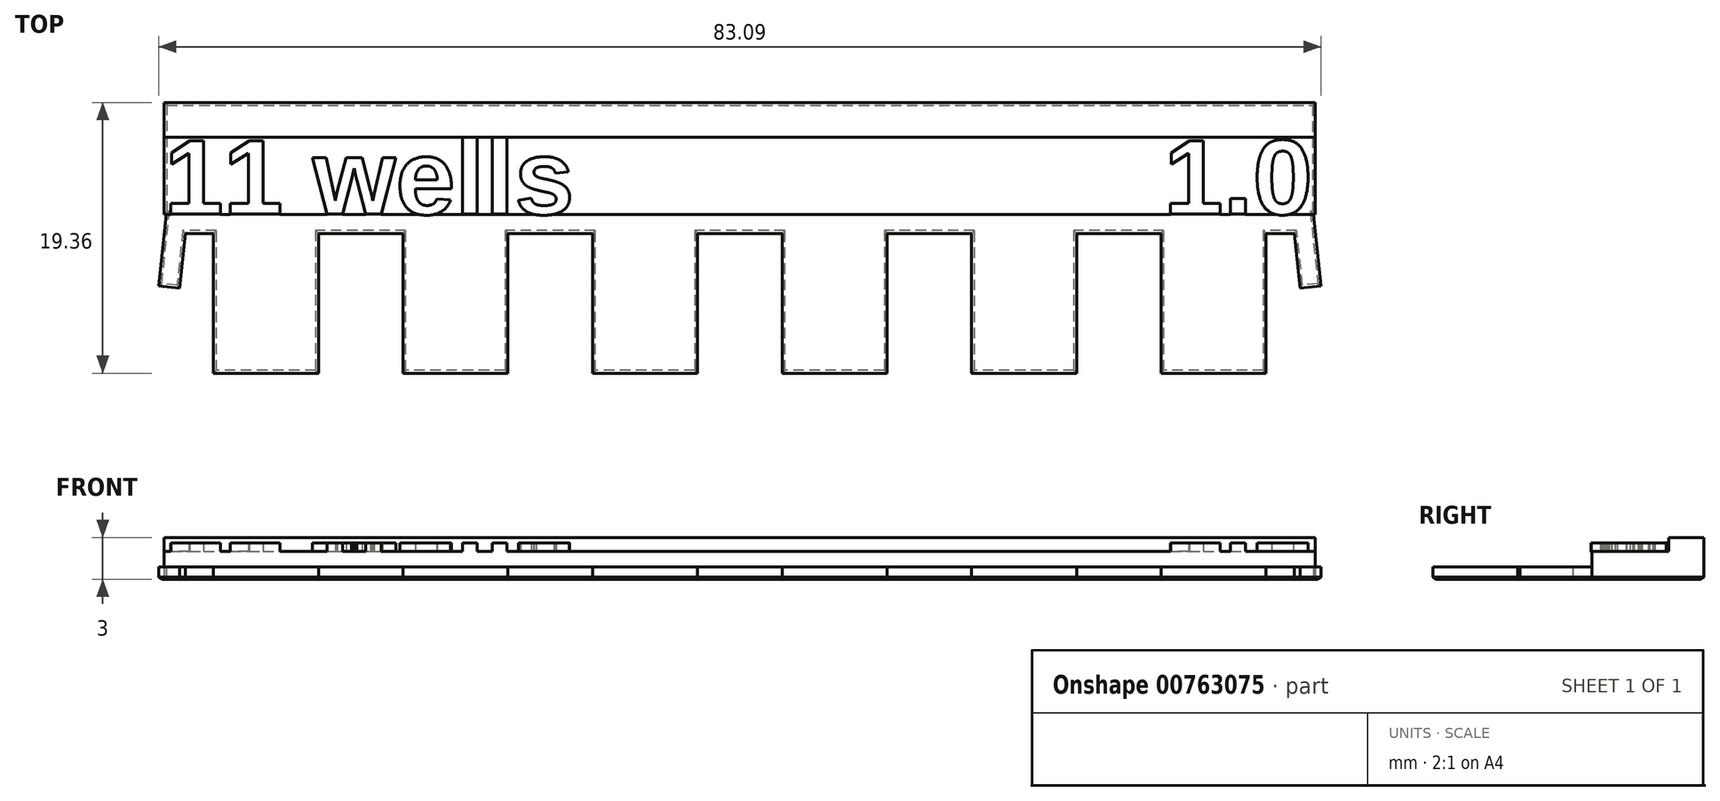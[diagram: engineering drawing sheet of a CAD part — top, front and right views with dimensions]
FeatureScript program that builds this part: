
annotation { "Feature Type Name" : "Feature", "Feature Type Description" : "" }
export const myFeature = defineFeature(function(context is Context, id is Id, definition is map)
    precondition{}
    {
        {
            assignVariable(context, id + "F0", {"name" : "thickness", "anyValue" : 0.9});
        }
        {
            var Q0;
            Q0=qCreatedBy(makeId("Top.planeOp"),FACE);
            var sketch = newSketch(context, id + "F1", { "sketchPlane" : qUnion([Q0])});
            skLineSegment(sketch, "E0", {"start": v(-32.04, 5.13) * mm, "end": v(-32.04, -4.87) * mm});
            skLineSegment(sketch, "E1", {"start": v(-32.04, -4.87) * mm, "end": v(-24.54, -4.87) * mm});
            skLineSegment(sketch, "E2", {"start": v(-24.54, -4.87) * mm, "end": v(-24.54, 5.13) * mm});
            skLineSegment(sketch, "E3", {"start": v(-24.54, 5.13) * mm, "end": v(-18.5, 5.13) * mm});
            skLineSegment(sketch, "E4", {"start": v(-35.57, 6.5) * mm, "end": v(46.73, 6.5) * mm});
            skLineSegment(sketch, "E5", {"start": v(-35.57, 12) * mm, "end": v(46.73, 12) * mm});
            skLineSegment(sketch, "E6", {"start": v(46.73, 14.5) * mm, "end": v(-35.57, 14.5) * mm});
            skLineSegment(sketch, "E7", {"start": v(-35.42, 6.5) * mm, "end": v(-35.57, 5.1) * mm});
            skLineSegment(sketch, "E8", {"start": v(-35.57, 5.1) * mm, "end": v(-35.96, 1.36) * mm});
            skLineSegment(sketch, "E9", {"start": v(-35.96, 1.36) * mm, "end": v(-34.47, 1.2) * mm});
            skLineSegment(sketch, "E10", {"start": v(5.58, 19.52) * mm, "end": v(5.58, -11.2) * mm, "construction": true});
            skLineSegment(sketch, "E11", {"start": v(-34.47, 1.2) * mm, "end": v(-34.05, 5.13) * mm});
            skLineSegment(sketch, "E12", {"start": v(-32.04, 5.13) * mm, "end": v(-34.05, 5.13) * mm});
            skLineSegment(sketch, "E13.1.0.0", {"start": v(-18.5, 5.13) * mm, "end": v(-18.5, -4.87) * mm});
            skLineSegment(sketch, "E13.1.0.1", {"start": v(-18.5, -4.87) * mm, "end": v(-11, -4.87) * mm});
            skLineSegment(sketch, "E13.1.0.2", {"start": v(-11, -4.87) * mm, "end": v(-11, 5.13) * mm});
            skLineSegment(sketch, "E13.1.0.3", {"start": v(-11, 5.13) * mm, "end": v(-4.94, 5.13) * mm});
            skLineSegment(sketch, "E13.2.0.0", {"start": v(-4.94, 5.13) * mm, "end": v(-4.94, -4.87) * mm});
            skLineSegment(sketch, "E13.2.0.1", {"start": v(-4.94, -4.87) * mm, "end": v(2.56, -4.87) * mm});
            skLineSegment(sketch, "E13.2.0.2", {"start": v(2.56, -4.87) * mm, "end": v(2.56, 5.13) * mm});
            skLineSegment(sketch, "E13.2.0.3", {"start": v(2.56, 5.13) * mm, "end": v(8.6, 5.13) * mm});
            skLineSegment(sketch, "E13.3.0.0", {"start": v(8.6, 5.13) * mm, "end": v(8.6, -4.87) * mm});
            skLineSegment(sketch, "E13.3.0.1", {"start": v(8.6, -4.87) * mm, "end": v(16.1, -4.87) * mm});
            skLineSegment(sketch, "E13.3.0.2", {"start": v(16.1, -4.87) * mm, "end": v(16.1, 5.13) * mm});
            skLineSegment(sketch, "E13.3.0.3", {"start": v(16.1, 5.13) * mm, "end": v(22.16, 5.13) * mm});
            skLineSegment(sketch, "E13.4.0.0", {"start": v(22.16, 5.13) * mm, "end": v(22.16, -4.87) * mm});
            skLineSegment(sketch, "E13.4.0.1", {"start": v(22.16, -4.87) * mm, "end": v(29.66, -4.87) * mm});
            skLineSegment(sketch, "E13.4.0.2", {"start": v(29.66, -4.87) * mm, "end": v(29.66, 5.13) * mm});
            skLineSegment(sketch, "E13.4.0.3", {"start": v(29.66, 5.13) * mm, "end": v(35.7, 5.13) * mm});
            skLineSegment(sketch, "E13.direction1", {"start": v(-32.04, -4.87) * mm, "end": v(-18.5, -4.87) * mm, "construction": true});
            skLineSegment(sketch, "E14", {"start": v(46.73, 6.5) * mm, "end": v(46.73, 14.5) * mm});
            skPoint(sketch, "E15", {"position": v(-35.57, 6.5) * mm});
            skLineSegment(sketch, "E16", {"start": v(-35.57, 12) * mm, "end": v(-35.57, 6.5) * mm});
            skLineSegment(sketch, "E17", {"start": v(-35.57, 12) * mm, "end": v(-35.57, 14.5) * mm});
            skLineSegment(sketch, "E18.MirrorCS", {"start": v(46.59, 6.5) * mm, "end": v(46.73, 5.1) * mm});
            skLineSegment(sketch, "E19.MirrorCS", {"start": v(46.73, 5.1) * mm, "end": v(47.13, 1.36) * mm});
            skLineSegment(sketch, "E20.MirrorCS", {"start": v(47.13, 1.36) * mm, "end": v(45.63, 1.2) * mm});
            skLineSegment(sketch, "E21.MirrorCS", {"start": v(45.63, 1.2) * mm, "end": v(45.22, 5.13) * mm});
            skLineSegment(sketch, "E22.MirrorCS", {"start": v(43.2, 5.13) * mm, "end": v(45.22, 5.13) * mm});
            skLineSegment(sketch, "E23.MirrorCS", {"start": v(43.2, 5.13) * mm, "end": v(43.2, -4.87) * mm});
            skLineSegment(sketch, "E24.MirrorCS", {"start": v(43.2, -4.87) * mm, "end": v(35.7, -4.87) * mm});
            skLineSegment(sketch, "E25.MirrorCS", {"start": v(35.7, -4.87) * mm, "end": v(35.7, 5.13) * mm});
            skSolve(sketch);
        }
        {
            var Q0;
            Q0=makeQuery(id+"F1.imprint","IMPRINT",FACE,{"disambiguationData":[TD([[makeQuery(id+"F1.imprint","IMPRINT",EDGE,{"derivedFrom":sQuery(id+"F1.wireOp",EDGE,"E0")}),1.0]])]});
            extrude(context, id + "F2", {"entities" : qUnion([Q0]), "depth" : (getVariable(context, 'thickness')) * mm, "offsetDistance" : 25 * mm});
        }
        {
            var Q0;
            {var subQ0=sQuery(id+"F1.wireOp",EDGE,"E5");Q0=makeQuery(id+"F1.imprint","IMPRINT",FACE,{"disambiguationData":[TD([[makeQuery(id+"F1.imprint","IMPRINT",EDGE,{"derivedFrom":subQ0}),-1.0]])]});}
            extrude(context, id + "F3", {"entities" : qUnion([Q0]), "operationType" : NewBodyOperationType.ADD, "depth" : 2 * mm, "offsetDistance" : 25 * mm});
        }
        {
            var Q0;
            {var subQ0=sQuery(id+"F1.wireOp",EDGE,"E5");Q0=makeQuery(id+"F1.imprint","IMPRINT",FACE,{"disambiguationData":[TD([[makeQuery(id+"F1.imprint","IMPRINT",EDGE,{"derivedFrom":subQ0}),1.0]])]});}
            extrude(context, id + "F4", {"entities" : qUnion([Q0]), "operationType" : NewBodyOperationType.ADD, "depth" : 3 * mm, "offsetDistance" : 25 * mm});
        }
        {
            var Q0;
            Q0=makeQuery(id+"F3.opExtrude","CAP_FACE",FACE,{"disambiguationData":[OSD([sQuery(id+"F1.wireOp",EDGE,"E4"),sQuery(id+"F1.wireOp",EDGE,"E5"),sQuery(id+"F1.wireOp",EDGE,"E14"),sQuery(id+"F1.wireOp",EDGE,"E16")])],"isStart":false});
            var sketch = newSketch(context, id + "F5", { "sketchPlane" : qUnion([Q0])});
            skText(sketch, "E26", { "text": "1.0", "fontName": "Arimo-Bold.ttf"});
            skText(sketch, "E27", { "text": "11 wells", "fontName": "Arimo-Bold.ttf"});
            const initialGuessF5  = {"E26": [0.0359, 0.0065, 1, 0, 0.0055], "E27": [-0.03557, 0.0065, 1, 0, 0.0055]};
            skSetInitialGuess(sketch, initialGuessF5);
            skSolve(sketch);
        }
        {
            var Q0;
            Q0 = qSketchRegion(id + "F5", true);
            extrude(context, id + "F6", {"entities" : qUnion([Q0]), "operationType" : NewBodyOperationType.ADD, "depth" : 0.6 * mm, "offsetDistance" : 25 * mm});
        }
        {
            var Q0;
            {var subQ0=sQuery(id+"F1.wireOp",EDGE,"E14");var subQ1=sQuery(id+"F1.wireOp",EDGE,"E5");var subQ2=sQuery(id+"F1.wireOp",EDGE,"E4");Q0=makeQuery(id+"F4.boolean.opBoolean","MERGE",FACE,{"derivedFrom":[makeQuery(id+"F3.boolean.opBoolean","MERGE",FACE,{"derivedFrom":[makeQuery(id+"F2.opExtrude","CAP_FACE",FACE,{"disambiguationData":[OSD([sQuery(id+"F1.wireOp",EDGE,"E0"),sQuery(id+"F1.wireOp",EDGE,"E1"),sQuery(id+"F1.wireOp",EDGE,"E2"),sQuery(id+"F1.wireOp",EDGE,"E3"),subQ2,sQuery(id+"F1.wireOp",EDGE,"E7"),sQuery(id+"F1.wireOp",EDGE,"E8"),sQuery(id+"F1.wireOp",EDGE,"E9"),sQuery(id+"F1.wireOp",EDGE,"E11"),sQuery(id+"F1.wireOp",EDGE,"E12"),sQuery(id+"F1.wireOp",EDGE,"E13.1.0.0"),sQuery(id+"F1.wireOp",EDGE,"E13.1.0.1"),sQuery(id+"F1.wireOp",EDGE,"E13.1.0.2"),sQuery(id+"F1.wireOp",EDGE,"E13.1.0.3"),sQuery(id+"F1.wireOp",EDGE,"E13.2.0.0"),sQuery(id+"F1.wireOp",EDGE,"E13.2.0.1"),sQuery(id+"F1.wireOp",EDGE,"E13.2.0.2"),sQuery(id+"F1.wireOp",EDGE,"E13.2.0.3"),sQuery(id+"F1.wireOp",EDGE,"E13.3.0.0"),sQuery(id+"F1.wireOp",EDGE,"E13.3.0.1"),sQuery(id+"F1.wireOp",EDGE,"E13.3.0.2"),sQuery(id+"F1.wireOp",EDGE,"E13.3.0.3"),sQuery(id+"F1.wireOp",EDGE,"E13.4.0.0"),sQuery(id+"F1.wireOp",EDGE,"E13.4.0.1"),sQuery(id+"F1.wireOp",EDGE,"E13.4.0.2"),sQuery(id+"F1.wireOp",EDGE,"E13.4.0.3"),sQuery(id+"F1.wireOp",EDGE,"E13.5.0.0"),sQuery(id+"F1.wireOp",EDGE,"E13.5.0.1"),sQuery(id+"F1.wireOp",EDGE,"E13.5.0.2"),sQuery(id+"F1.wireOp",EDGE,"E13.5.0.3"),sQuery(id+"F1.wireOp",EDGE,"E13.6.0.0"),sQuery(id+"F1.wireOp",EDGE,"E13.6.0.1"),sQuery(id+"F1.wireOp",EDGE,"E13.6.0.2"),sQuery(id+"F1.wireOp",EDGE,"E13.6.0.3"),sQuery(id+"F1.wireOp",EDGE,"E13.7.0.0"),sQuery(id+"F1.wireOp",EDGE,"E13.7.0.1"),sQuery(id+"F1.wireOp",EDGE,"E13.7.0.2"),sQuery(id+"F1.wireOp",EDGE,"E13.7.0.3"),sQuery(id+"F1.wireOp",EDGE,"E13.8.0.0"),sQuery(id+"F1.wireOp",EDGE,"E13.8.0.1"),sQuery(id+"F1.wireOp",EDGE,"E13.8.0.2"),sQuery(id+"F1.wireOp",EDGE,"E13.8.0.3"),sQuery(id+"F1.wireOp",EDGE,"E13.9.0.0"),sQuery(id+"F1.wireOp",EDGE,"E13.9.0.1"),sQuery(id+"F1.wireOp",EDGE,"E13.9.0.2"),sQuery(id+"F1.wireOp",EDGE,"E13.9.0.3"),sQuery(id+"F1.wireOp",EDGE,"E18.MirrorCS"),sQuery(id+"F1.wireOp",EDGE,"E19.MirrorCS"),sQuery(id+"F1.wireOp",EDGE,"E20.MirrorCS"),sQuery(id+"F1.wireOp",EDGE,"E21.MirrorCS"),sQuery(id+"F1.wireOp",EDGE,"E22.MirrorCS"),sQuery(id+"F1.wireOp",EDGE,"E23.MirrorCS"),sQuery(id+"F1.wireOp",EDGE,"E24.MirrorCS"),sQuery(id+"F1.wireOp",EDGE,"E25.MirrorCS"),sQuery(id+"F1.wireOp",EDGE,"e45c2a3d-9124-456e-8a19-0788b070fa31.0.10.0"),sQuery(id+"F1.wireOp",EDGE,"e45c2a3d-9124-456e-8a19-0788b070fa31.3.10.0"),sQuery(id+"F1.wireOp",EDGE,"e45c2a3d-9124-456e-8a19-0788b070fa31.6.10.0"),sQuery(id+"F1.wireOp",EDGE,"e45c2a3d-9124-456e-8a19-0788b070fa31.9.10.0"),sQuery(id+"F1.wireOp",EDGE,"e45c2a3d-9124-456e-8a19-0788b070fa31.0.11.0"),sQuery(id+"F1.wireOp",EDGE,"e45c2a3d-9124-456e-8a19-0788b070fa31.3.11.0"),sQuery(id+"F1.wireOp",EDGE,"e45c2a3d-9124-456e-8a19-0788b070fa31.6.11.0"),sQuery(id+"F1.wireOp",EDGE,"e45c2a3d-9124-456e-8a19-0788b070fa31.9.11.0")])],"isStart":true}),makeQuery(id+"F3.opExtrude","CAP_FACE",FACE,{"disambiguationData":[OSD([subQ2,subQ1,subQ0,sQuery(id+"F1.wireOp",EDGE,"E16")])],"isStart":true})]}),makeQuery(id+"F4.opExtrude","CAP_FACE",FACE,{"disambiguationData":[OSD([subQ1,sQuery(id+"F1.wireOp",EDGE,"E6"),subQ0,sQuery(id+"F1.wireOp",EDGE,"E17")])],"isStart":true})]});}
            chamfer(context, id + "F7", {"entities" : qUnion([Q0]), "chamferType" : ChamferType.TWO_OFFSETS, "width1" : 0.15 * mm, "oppositeDirection" : false, "width2" : 0.2 * mm, "tangentPropagation" : true});
        }
    });
